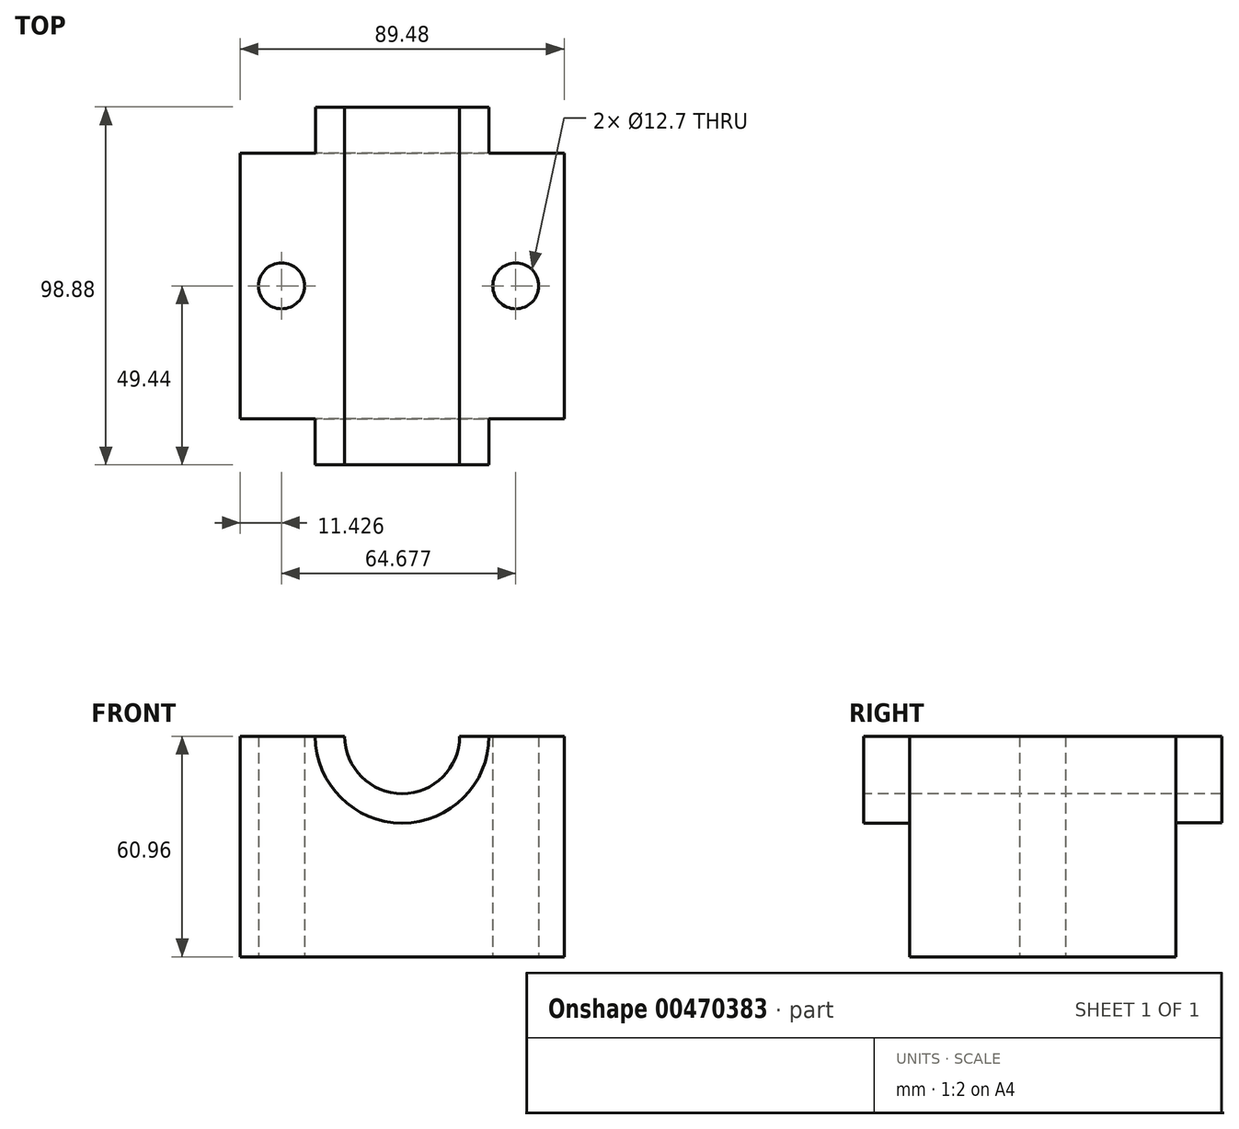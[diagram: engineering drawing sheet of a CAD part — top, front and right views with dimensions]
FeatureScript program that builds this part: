
annotation { "Feature Type Name" : "Feature", "Feature Type Description" : "" }
export const myFeature = defineFeature(function(context is Context, id is Id, definition is map)
    precondition{}
    {
        {
            var Q0;
            Q0=qCreatedBy(makeId("Top.planeOp"),FACE);
            var sketch = newSketch(context, id + "F0", { "sketchPlane" : qUnion([Q0])});
            skLineSegment(sketch, "E0.bottom", {"start": v(-44.74, 36.74) * mm, "end": v(44.74, 36.74) * mm});
            skLineSegment(sketch, "E0.top", {"start": v(-44.74, -36.74) * mm, "end": v(44.74, -36.74) * mm});
            skLineSegment(sketch, "E0.left", {"start": v(-44.74, 36.74) * mm, "end": v(-44.74, -36.74) * mm});
            skLineSegment(sketch, "E0.right", {"start": v(44.74, 36.74) * mm, "end": v(44.74, -36.74) * mm});
            skPoint(sketch, "E0.middle", {"position": v(0, 0) * mm});
            skSolve(sketch);
        }
        {
            var Q0;
            Q0=makeQuery(id+"F0.imprint","IMPRINT",FACE,{"disambiguationData":[TD([[makeQuery(id+"F0.imprint","IMPRINT",EDGE,{"derivedFrom":sQuery(id+"F0.wireOp",EDGE,"E0.bottom")}),-1.0]])]});
            extrude(context, id + "F1", {"entities" : qUnion([Q0]), "depth" : 60.96 * mm});
        }
        {
            var Q0;
            Q0=makeQuery(id+"F1.opExtrude","CAP_FACE",FACE,{"disambiguationData":[OSD([sQuery(id+"F0.wireOp",EDGE,"E0.bottom"),sQuery(id+"F0.wireOp",EDGE,"E0.top"),sQuery(id+"F0.wireOp",EDGE,"E0.left"),sQuery(id+"F0.wireOp",EDGE,"E0.right")])],"isStart":true});
            var sketch = newSketch(context, id + "F2", { "sketchPlane" : qUnion([Q0])});
            skPoint(sketch, "E1", {"position": v(-33.31, 0) * mm});
            skPoint(sketch, "E2", {"position": v(31.36, 0) * mm});
            skSolve(sketch);
        }
        {
            var Q0;
            Q0=sQuery(id+"F2.wireOp",VERTEX,"E1");
            var Q1;
            Q1=sQuery(id+"F2.wireOp",VERTEX,"E2");
            var Q2;
            Q2=makeQuery(id+"F1.opExtrude","SWEPT_BODY",BODY,{"disambiguationData":[OSD([sQuery(id+"F0.wireOp",EDGE,"E0.bottom"),sQuery(id+"F0.wireOp",EDGE,"E0.top"),sQuery(id+"F0.wireOp",EDGE,"E0.left"),sQuery(id+"F0.wireOp",EDGE,"E0.right")])]});
            hole(context, id + "F3", {"style" : HoleStyle.SIMPLE, "endStyle" : HoleEndStyle.THROUGH, "holeDiameter" : 12.7 * mm, "isTappedThrough" : true, "tappedDepth" : 12.7 * mm, "tapClearance" : 3, "locations" : qUnion([Q0, Q1]), "scope" : qUnion([Q2])});
        }
        {
            var Q0;
            Q0=makeQuery(id+"F1.opExtrude","SWEPT_FACE",FACE,{"disambiguationData":[OSD([sQuery(id+"F0.wireOp",EDGE,"E0.top")])]});
            var sketch = newSketch(context, id + "F4", { "sketchPlane" : qUnion([Q0])});
            skPoint(sketch, "E3", {"position": v(0, 60.96) * mm});
            skArc(sketch, "E4", {"start": v(-21.75, 60.96) * mm, "mid": v(0, 39.2) * mm, "end": v(21.75, 60.96) * mm});
            skPoint(sketch, "E5", {"position": v(-21.75, 60.96) * mm});
            skPoint(sketch, "E6", {"position": v(21.75, 60.96) * mm});
            skSolve(sketch);
        }
        {
            var Q0;
            Q0=sQuery(id+"F4.wireOp",VERTEX,"E3");
            var Q1;
            Q1=makeQuery(id+"F1.opExtrude","SWEPT_BODY",BODY,{"disambiguationData":[OSD([sQuery(id+"F0.wireOp",EDGE,"E0.bottom"),sQuery(id+"F0.wireOp",EDGE,"E0.top"),sQuery(id+"F0.wireOp",EDGE,"E0.left"),sQuery(id+"F0.wireOp",EDGE,"E0.right")])]});
            hole(context, id + "F5", {"style" : HoleStyle.SIMPLE, "endStyle" : HoleEndStyle.THROUGH, "holeDiameter" : 31.75 * mm, "isTappedThrough" : true, "tappedDepth" : 12.7 * mm, "tapClearance" : 3, "locations" : qUnion([Q0]), "scope" : qUnion([Q1])});
        }
        {
            var Q0;
            Q0=makeQuery(id+"F1.opExtrude","SWEPT_FACE",FACE,{"disambiguationData":[OSD([sQuery(id+"F0.wireOp",EDGE,"E0.top")])]});
            var sketch = newSketch(context, id + "F6", { "sketchPlane" : qUnion([Q0])});
            skArc(sketch, "E7", {"start": v(-24, 60.96) * mm, "mid": v(0, 36.96) * mm, "end": v(24, 60.96) * mm});
            skPoint(sketch, "E8", {"position": v(-24, 60.96) * mm});
            skPoint(sketch, "E9", {"position": v(-15.88, 60.96) * mm});
            skPoint(sketch, "E10", {"position": v(15.87, 60.96) * mm});
            skPoint(sketch, "E11", {"position": v(24, 60.96) * mm});
            skSolve(sketch);
        }
        {
            var Q0;
            Q0 = qSketchRegion(id + "F6", true);
            var Q1;
            {var subQ0=sQuery(id+"F6.wireOp",EDGE,"E7");Q1=makeQuery(id+"F6.imprint","IMPRINT",FACE,{"disambiguationData":[TD([[makeQuery(id+"F6.imprint","IMPRINT",EDGE,{"derivedFrom":subQ0}),1.0]])]});}
            extrude(context, id + "F7", {"entities" : qUnion([Q0, Q1]), "operationType" : NewBodyOperationType.ADD, "depth" : 25.4 * mm, "symmetric" : true});
        }
        {
            var Q0;
            Q0=makeQuery(id+"F1.opExtrude","SWEPT_FACE",FACE,{"disambiguationData":[OSD([sQuery(id+"F0.wireOp",EDGE,"E0.bottom")])]});
            var sketch = newSketch(context, id + "F8", { "sketchPlane" : qUnion([Q0])});
            skArc(sketch, "E12", {"start": v(-23.97, 60.96) * mm, "mid": v(0, 36.99) * mm, "end": v(23.97, 60.96) * mm});
            skPoint(sketch, "E13", {"position": v(-15.87, 60.96) * mm});
            skPoint(sketch, "E14", {"position": v(-23.97, 60.96) * mm});
            skPoint(sketch, "E15", {"position": v(15.87, 60.96) * mm});
            skPoint(sketch, "E16", {"position": v(23.97, 60.96) * mm});
            skSolve(sketch);
        }
        {
            var Q0;
            Q0 = qSketchRegion(id + "F8", true);
            var Q1;
            {var subQ0=sQuery(id+"F8.wireOp",EDGE,"E12");Q1=makeQuery(id+"F8.imprint","IMPRINT",FACE,{"disambiguationData":[TD([[makeQuery(id+"F8.imprint","IMPRINT",EDGE,{"derivedFrom":subQ0}),1.0]])]});}
            extrude(context, id + "F9", {"entities" : qUnion([Q0, Q1]), "operationType" : NewBodyOperationType.ADD, "depth" : 25.4 * mm, "symmetric" : true});
        }
    });
